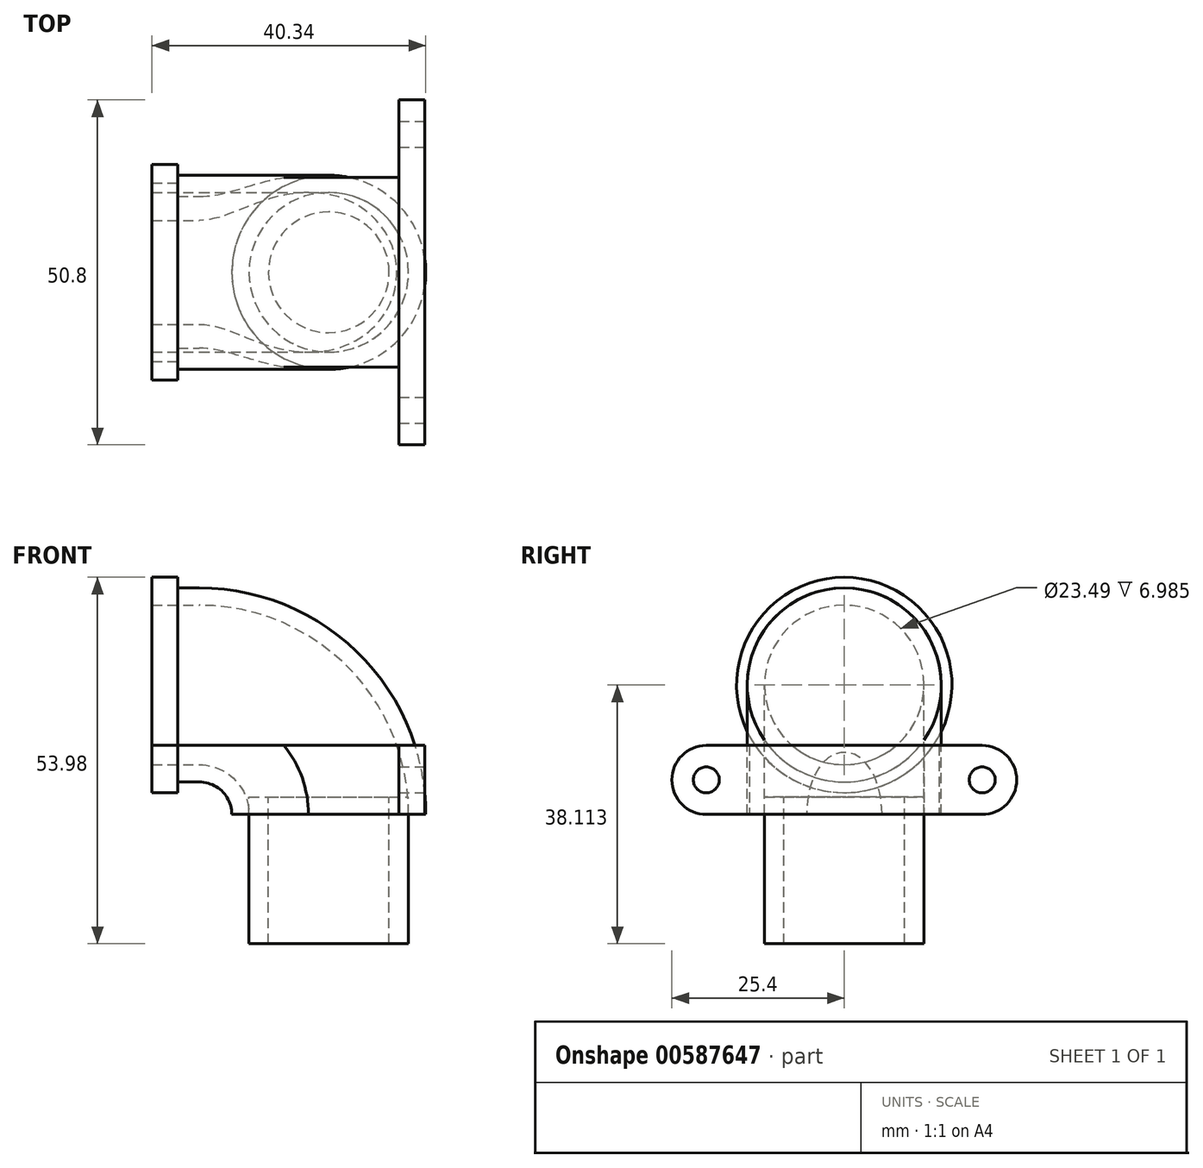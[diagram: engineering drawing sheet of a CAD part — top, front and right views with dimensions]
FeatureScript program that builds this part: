
annotation { "Feature Type Name" : "Feature", "Feature Type Description" : "" }
export const myFeature = defineFeature(function(context is Context, id is Id, definition is map)
    precondition{}
    {
        {
            var Q0;
            Q0=qCreatedBy(makeId("Front.planeOp"),FACE);
            var sketch = newSketch(context, id + "F0", { "sketchPlane" : qUnion([Q0])});
            skArc(sketch, "E0", {"start": v(0, 33.35) * mm, "mid": v(23.58, 23.58) * mm, "end": v(33.35, 0) * mm});
            skSolve(sketch);
        }
        {
            var Q0;
            Q0=qCreatedBy(makeId("Right.planeOp"),FACE);
            var sketch = newSketch(context, id + "F1", { "sketchPlane" : qUnion([Q0])});
            skCircle(sketch, "E1", {"center": v(0, 19.06) * mm, "radius": 14.29 * mm});
            skCircle(sketch, "E2", {"center": v(0, 19.06) * mm, "radius": 11.75 * mm});
            skSolve(sketch);
        }
        {
            var Q0;
            Q0=makeQuery(id+"F1.imprint","IMPRINT",FACE,{"disambiguationData":[TD([[makeQuery(id+"F1.imprint","IMPRINT",EDGE,{"derivedFrom":sQuery(id+"F1.wireOp",EDGE,"E1")}),1.0]])]});
            var Q1;
            Q1=sQuery(id+"F0.wireOp",EDGE,"E0");
            sweep(context, id + "F2", {"profiles" : qUnion([Q0]), "path" : qUnion([Q1])});
        }
        {
            var Q0;
            Q0=makeQuery(id+"F2.opSweep","CAP_FACE",FACE,{"disambiguationData":[OSD([sQuery(id+"F0.wireOp",VERTEX,"E0.end"),sQuery(id+"F1.wireOp",EDGE,"E1"),sQuery(id+"F1.wireOp",EDGE,"E2")])],"isStart":false});
            var sketch = newSketch(context, id + "F3", { "sketchPlane" : qUnion([Q0])});
            skCircle(sketch, "E3.0", {"center": v(19.06, 0) * mm, "radius": 11.75 * mm});
            skCircle(sketch, "E4", {"center": v(19.06, 0) * mm, "radius": 8.9 * mm});
            skSolve(sketch);
        }
        {
            var Q0;
            Q0=makeQuery(id+"F3.imprint","IMPRINT",FACE,{"disambiguationData":[TD([[makeQuery(id+"F3.imprint","IMPRINT",EDGE,{"derivedFrom":sQuery(id+"F3.wireOp",EDGE,"E3.0")}),1.0]])]});
            extrude(context, id + "F4", {"entities" : qUnion([Q0]), "depth" : 19.05 * mm, "offsetDistance" : 25.4 * mm, "hasSecondDirection" : true, "secondDirectionOppositeDirection" : true, "secondDirectionDepth" : 2.54 * mm});
        }
        {
            var Q0;
            Q0=qCreatedBy(makeId("Front.planeOp"),FACE);
            var sketch = newSketch(context, id + "F5", { "sketchPlane" : qUnion([Q0])});
            skLineSegment(sketch, "E5.0", {"start": v(0, 33.35) * mm, "end": v(0, 4.78) * mm, "construction": true});
            skLineSegment(sketch, "E6", {"start": v(0, 33.35) * mm, "end": v(-3.17, 33.35) * mm});
            skLineSegment(sketch, "E7", {"start": v(-3.17, 33.35) * mm, "end": v(-3.17, 34.93) * mm});
            skLineSegment(sketch, "E8", {"start": v(-3.18, 34.93) * mm, "end": v(-6.99, 34.93) * mm});
            skLineSegment(sketch, "E9", {"start": v(-6.99, 34.93) * mm, "end": v(-6.99, 30.81) * mm});
            skLineSegment(sketch, "E10", {"start": v(-6.99, 30.81) * mm, "end": v(0, 30.81) * mm});
            skLineSegment(sketch, "E11", {"start": v(0, 30.81) * mm, "end": v(0, 33.35) * mm});
            skLineSegment(sketch, "E12", {"start": v(0, 19.06) * mm, "end": v(-13.12, 19.06) * mm, "construction": true});
            skSolve(sketch);
        }
        {
            var Q0;
            Q0 = qSketchRegion(id + "F5", true);
            var Q1;
            Q1=sQuery(id+"F5.wireOp",EDGE,"E12");
            revolve(context, id + "F6", {"operationType" : NewBodyOperationType.ADD, "entities" : qUnion([Q0]), "axis" : qUnion([Q1]), "revolveType" : RevolveType.FULL});
        }
        {
            var Q0;
            Q0=qCreatedBy(makeId("Right.planeOp"),FACE);
            cPlane(context, id + "F7", {"entities" : qUnion([Q0]), "cplaneType" : CPlaneType.OFFSET, "offset" : 33.22 * mm, "width" : 152.4 * mm, "height" : 152.4 * mm});
        }
        {
            var Q0;
            Q0=qCreatedBy(id+"F7.planeOp",FACE);
            var sketch = newSketch(context, id + "F8", { "sketchPlane" : qUnion([Q0])});
            skLineSegment(sketch, "E13", {"start": v(-27.25, 5.08) * mm, "end": v(24.29, 5.08) * mm, "construction": true});
            skLineSegment(sketch, "E14", {"start": v(0, 11.17) * mm, "end": v(0, -24.77) * mm, "construction": true});
            skLineSegment(sketch, "E15", {"start": v(-20.32, 0) * mm, "end": v(20.32, 0) * mm});
            skLineSegment(sketch, "E16", {"start": v(-20.32, 10.16) * mm, "end": v(20.32, 10.16) * mm});
            skPoint(sketch, "E17", {"position": v(-20.32, 5.08) * mm});
            skPoint(sketch, "E18", {"position": v(20.32, 5.08) * mm});
            skLineSegment(sketch, "E19", {"start": v(-20.32, 12.41) * mm, "end": v(-20.32, -5.27) * mm, "construction": true});
            skLineSegment(sketch, "E20", {"start": v(20.32, 12.28) * mm, "end": v(20.32, -6.05) * mm, "construction": true});
            skArc(sketch, "E21", {"start": v(-20.32, 0) * mm, "mid": v(-25.4, 5.08) * mm, "end": v(-20.32, 10.16) * mm});
            skArc(sketch, "E22", {"start": v(20.32, 10.16) * mm, "mid": v(25.4, 5.08) * mm, "end": v(20.32, 0) * mm});
            skCircle(sketch, "E23", {"center": v(-20.32, 5.08) * mm, "radius": 1.9 * mm});
            skCircle(sketch, "E24", {"center": v(20.32, 5.08) * mm, "radius": 1.9 * mm});
            skSolve(sketch);
        }
        {
            var Q0;
            Q0=makeQuery(id+"F8.imprint","IMPRINT",FACE,{"disambiguationData":[TD([[makeQuery(id+"F8.imprint","IMPRINT",EDGE,{"derivedFrom":sQuery(id+"F8.wireOp",EDGE,"E15")}),1.0]])]});
            extrude(context, id + "F9", {"entities" : qUnion([Q0]), "oppositeDirection" : true, "depth" : 3.8 * mm, "offsetDistance" : 25.4 * mm});
        }
        {
            var Q0;
            Q0=makeQuery(id+"F9.opExtrude","CAP_FACE",FACE,{"disambiguationData":[OSD([sQuery(id+"F8.wireOp",EDGE,"E15"),sQuery(id+"F8.wireOp",EDGE,"E16"),sQuery(id+"F8.wireOp",EDGE,"E21"),sQuery(id+"F8.wireOp",EDGE,"E22"),sQuery(id+"F8.wireOp",EDGE,"E23"),sQuery(id+"F8.wireOp",EDGE,"E24")])],"isStart":false});
            var sketch = newSketch(context, id + "F10", { "sketchPlane" : qUnion([Q0])});
            skLineSegment(sketch, "E25.bottom", {"start": v(13.97, 10.16) * mm, "end": v(-13.97, 10.16) * mm});
            skLineSegment(sketch, "E25.top", {"start": v(13.97, 0) * mm, "end": v(-13.97, 0) * mm});
            skLineSegment(sketch, "E25.left", {"start": v(13.97, 10.16) * mm, "end": v(13.97, 0) * mm});
            skLineSegment(sketch, "E25.right", {"start": v(-13.97, 10.16) * mm, "end": v(-13.97, 0) * mm});
            skLineSegment(sketch, "E26", {"start": v(0, 0) * mm, "end": v(0, 15.48) * mm, "construction": true});
            skSolve(sketch);
        }
        {
            var Q0;
            Q0 = qSketchRegion(id + "F10", true);
            extrude(context, id + "F11", {"entities" : qUnion([Q0]), "endBound" : BoundingType.UP_TO_NEXT, "depth" : 25.4 * mm, "offsetDistance" : 25.4 * mm});
        }
    });
